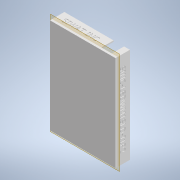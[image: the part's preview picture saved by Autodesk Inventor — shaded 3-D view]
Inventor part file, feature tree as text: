
AUTODESK INVENTOR PART (.ipt)
format: ipt  version: 2020 (Build 240168000, 168)  size: 643,072 bytes
history: native  units: in
note: dims shown in document units (in); Inventor stores cm internally (conversion verified against a paired STEP export)
features: extrude x8, sketch x8, other x3, plane x1
ambient origin geometry x8: Origin, YZ Plane, XZ Plane, XY Plane, X Axis, Y Axis, Z Axis, Center Point
bodies: Solid1 (feature_tree)
feature tree (20):
  plane  "Work Plane1"
  extrude  "Extrusion1"  Depth=0.0232in TaperAngle=0.0deg
  extrude  "Extrusion2"  Depth=0.3937in TaperAngle=0.0deg
  extrude  "Extrusion3"  Depth=0.0591in
  extrude  "Extrusion4"  Depth=0.0591in
  extrude  "Extrusion6"  Depth=0.1772in TaperAngle=0.0deg
  extrude  "Extrusion5"  Depth=0.0276in TaperAngle=0.0deg
  extrude  "Extrusion7"  [1 undecoded]
  extrude  "Extrusion8"  [1 undecoded]
  sketch  "Sketch1"  dims[d0=0.0812in d1=0.5719in d2=0.0in d3=0.0in d4=0.0232in d5=0.0in]
  sketch  "Sketch2"  dims[d6=0.0232in d7=0.0in d8=0.3937in d9=0.0in]
  sketch  "Sketch3"  dims[d10=0.1772in d11=0.0in d12=0.0591in]
  sketch  "Sketch4"  dims[d13=0.0591in d14=0.0591in]
  sketch  "Sketch5"  dims[d15=0.0591in d16=0.1772in d17=0.0in]
  sketch  "Sketch6"  dims[d18=0.0276in d19=0.0in d20=0.0276in d21=0.0in]
  sketch  "Sketch7"
  sketch  "Sketch8"
  parser-record x1  (decoder bookkeeping rows leaked as tree rows — omitted from the tree; the rows remain in map.json)
  other  "I0020.iam"
  other  "Buttom Case:1"
note: 2 required parameter values undecoded (feature->parameter linkage not recoverable at this tier; creation-order binding heuristic only, values carry confidence <= 0.55)
note: 1 file-system path scrubbed to <path> (originals preserved in map.json)
